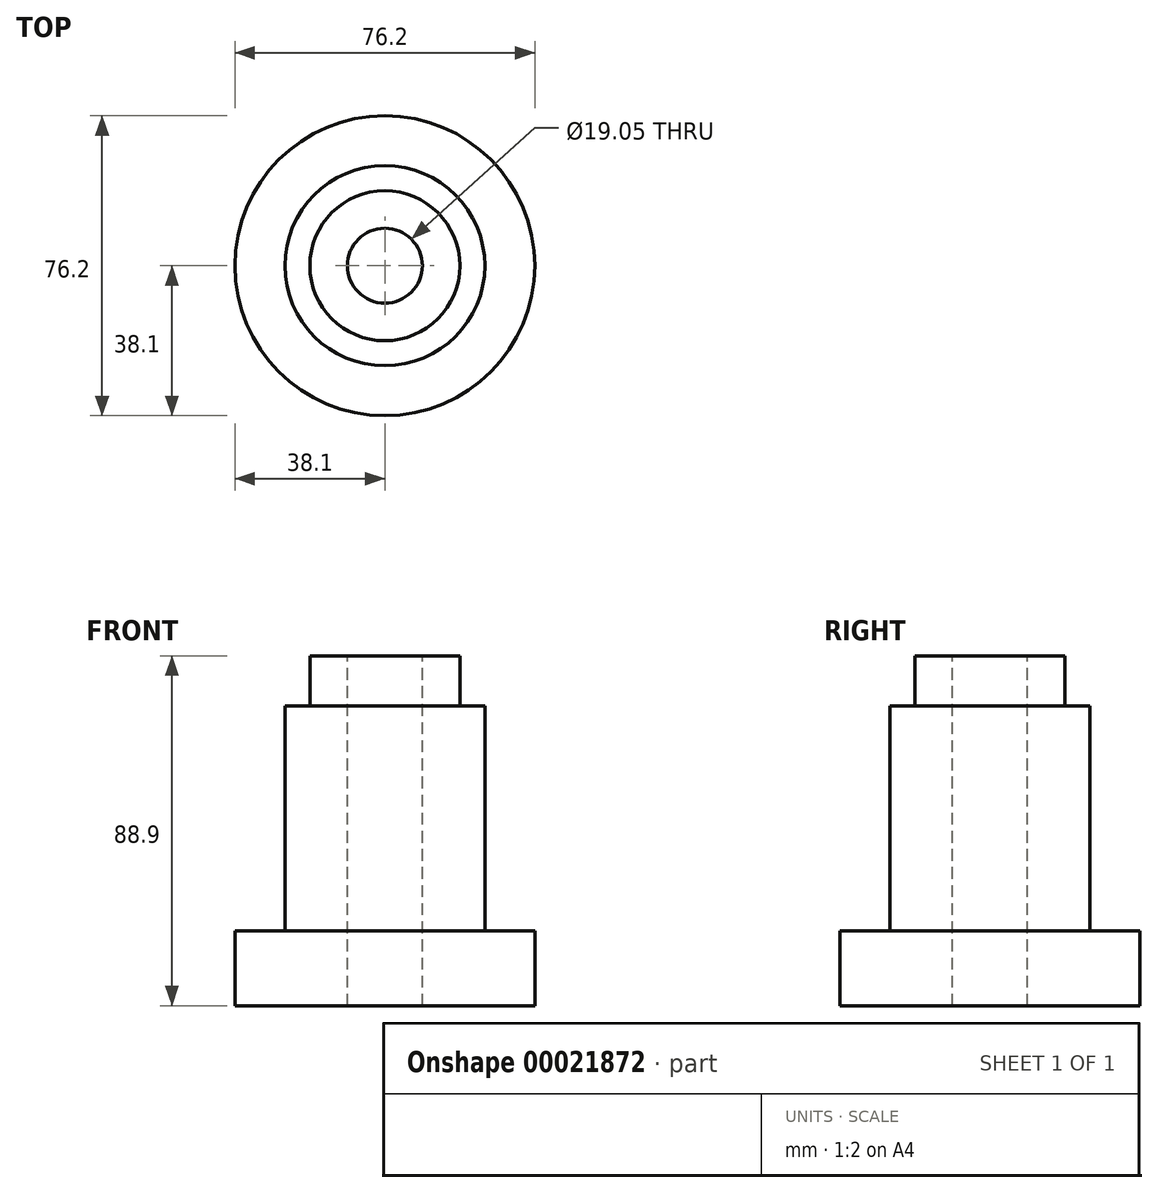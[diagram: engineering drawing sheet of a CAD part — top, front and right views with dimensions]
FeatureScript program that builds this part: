
annotation { "Feature Type Name" : "Feature", "Feature Type Description" : "" }
export const myFeature = defineFeature(function(context is Context, id is Id, definition is map)
    precondition{}
    {
        {
            var Q0;
            Q0=qCreatedBy(makeId("Front.planeOp"),FACE);
            var sketch = newSketch(context, id + "F0", { "sketchPlane" : qUnion([Q0])});
            skLineSegment(sketch, "E0", {"start": v(0, -41.89) * mm, "end": v(38.1, -41.89) * mm});
            skLineSegment(sketch, "E1", {"start": v(38.1, -41.89) * mm, "end": v(38.1, -22.84) * mm});
            skLineSegment(sketch, "E2", {"start": v(38.1, -22.84) * mm, "end": v(25.4, -22.84) * mm});
            skLineSegment(sketch, "E3", {"start": v(25.4, -22.84) * mm, "end": v(25.4, 34.31) * mm});
            skLineSegment(sketch, "E4", {"start": v(25.4, 34.31) * mm, "end": v(19.05, 34.31) * mm});
            skLineSegment(sketch, "E5", {"start": v(19.05, 34.31) * mm, "end": v(19.05, 47.01) * mm});
            skLineSegment(sketch, "E6", {"start": v(19.05, 47.01) * mm, "end": v(0, 47.01) * mm});
            skLineSegment(sketch, "E7", {"start": v(0, 47.01) * mm, "end": v(0, -41.89) * mm});
            skSolve(sketch);
        }
        {
            var Q0;
            Q0=makeQuery(id+"F0.imprint","IMPRINT",FACE,{"disambiguationData":[TD([[makeQuery(id+"F0.imprint","IMPRINT",EDGE,{"derivedFrom":sQuery(id+"F0.wireOp",EDGE,"E0")}),1.0]])]});
            var Q1;
            Q1=sQuery(id+"F0.wireOp",EDGE,"E7");
            revolve(context, id + "F1", {"entities" : qUnion([Q0]), "axis" : qUnion([Q1]), "revolveType" : RevolveType.FULL});
        }
        {
            var Q0;
            Q0=makeQuery(id+"F1.opRevolve","SWEPT_FACE",FACE,{"disambiguationData":[OSD([sQuery(id+"F0.wireOp",EDGE,"E6")])]});
            var sketch = newSketch(context, id + "F2", { "sketchPlane" : qUnion([Q0])});
            skCircle(sketch, "E8", {"center": v(0, 0) * mm, "radius": 9.53 * mm});
            skLineSegment(sketch, "E9", {"start": v(0, 9.52) * mm, "end": v(0, -9.52) * mm});
            skSolve(sketch);
        }
        {
            var Q0;
            {var subQ0=sQuery(id+"F2.wireOp",EDGE,"E9");Q0=makeQuery(id+"F2.imprint","IMPRINT",FACE,{"disambiguationData":[TD([[makeQuery(id+"F2.imprint","IMPRINT",EDGE,{"derivedFrom":subQ0}),-1.0]])]});}
            var Q1;
            {var subQ0=sQuery(id+"F2.wireOp",EDGE,"E9");Q1=makeQuery(id+"F2.imprint","IMPRINT",FACE,{"disambiguationData":[TD([[makeQuery(id+"F2.imprint","IMPRINT",EDGE,{"derivedFrom":subQ0}),1.0]])]});}
            extrude(context, id + "F3", {"entities" : qUnion([Q0, Q1]), "operationType" : NewBodyOperationType.REMOVE, "oppositeDirection" : true, "depth" : 180.66 * mm});
        }
    });
